# Revit family: Plymold-Aurora-Dining_Height-Table_Base
name_source: partatom
category: Furniture
units: mm (PartAtom-declared; Revit-internal decimal feet)

## family parameters
Always vertical = Yes
Cut with Voids When Loaded = No
OmniClass Number = 23.40.20.00
OmniClass Title = General Furniture and Specialties
Render Appearance Source = Family Geometry
Room Calculation Point = No
Shared = Yes
Work Plane-Based = No

## types (4) — shared parameters
Assembly Code = E2020200
Default Elevation = 0"
Depth = 11"
Keynote = 12500
Manufacturer = Plymold Inc.
Product Documentation Link = https://plymold.com
Revit Model Built By = https://www.servex-us.com
Sustainability = https://plymold.com
Type Comments = Aurora
URL = https://plymold.com
Width = 11"
zero-valued in all types: Cost

## per-type parameters (varying)
| type | Bolt Down | Description | Dist Leg | Dist Void | FRAME MATERIAL | Grout In | Height |
| 70709AL03 | No | Grout In - Onyx Black - 11"W x11"D x 34.25"H | 0" | 1" | PLY - Onyx Black Powdercoat | Yes | 34 1/4" |
| 70709AL02 | No | Grout In - Iron Glimmer - 11"W x11"D x 34.25"H | 0" | 1" | PLY - Iron Glimme Powdercoat | Yes | 34 1/4" |
| 70609AL03 | Yes | Bolt Down - Onyx Black - 11"W x11"D x 34.25"H | 5 5/8" | 0" | PLY - Onyx Black Powdercoat | No | 28 1/4" |
| 70609AL02 | Yes | Bolt Down - Iron Glimme - 11"W x11"D x 34.25"H | 5 5/8" | 0" | PLY - Iron Glimme Powdercoat | No | 28 1/4" |

note: column(s) folded — value = type name in every type: Model

## geometry (parser evidence)
native form markers: Sweep x4
no freeform markers — native parametric forms only
